# Revit family: ASH_Contour21_S6360_BIM_GB
name_source: partatom
category: Plumbing Fixtures
revit_build: Autodesk Revit MEP 2012 (Build: 20110309_2315(x64)
units: mm (PartAtom-declared; Revit-internal decimal feet)

## types (5) — shared parameters
AccessibilityPerformance = DDA Compliant
Accessories = www.idealspec.co.uk
Assembly Code = C1030200
AssetType = Fixed
BIMObjectName = GRABRAIL_ArmitageShanks_Contour21-Hinged80cm_S6360
Brand = Armitage Shanks
Category = Furntiure_GRABRAIL_UK
ConnectionType = Mechanical
CurrentRevision = 1
Default Elevation = 1219 mm
Description = Contour 21 hinged support rail 80 x 35mm diameter, Doc M Compliant
DurationUnit = Years
ElementType = GRAB RAIL: Safety device to aid maintaining balance, lessen fatigue and assist in supporting weight whilst maneuvering the body
ExpectedLife = 30
Help = http://www.idealspec.co.uk
InstallationInstructions = http://www.idealspec.co.uk
Manufacturer = Ideal Standard International Ltd
ManufacturerURL = www.idealspec.co.uk
Name = GRABRAIL_ArmitageShanks_Contour21-Hinged80cm_S6360
NettWeight = 3.15Kg
NominalHeight = 201 mm
NominalLength = 800 mm  [stored 2.62467 ft]
NominalWidth = 107 mm  [stored 0.35105 ft]
PredefinedType = grabrail
ProductDataSheet = http://www.idealspec.co.uk
ProductInformation = http://www.idealspec.co.uk
S6363AC Required = Yes
SalesInformation = http://www.idealspec.co.uk
SendEnquiry = http://www.idealspec.co.uk
Shape = Tubular
Size = 800mm x 100mm x 200mm
Space = Internal
SpareParts = www.fastpart-spares.co.uk
StandardsConformance = DDA, Doc-M
URL = www.idealspec.co.uk
Version = 2
VolumeUnits = Litres
WarrantyDescription = Manufacturers Warranty
WarrantyDurationParts = 5
WarrantyDurationUnit = Years
WarrantyGuarantorParts = Ideal Standard International Ltd

## per-type parameters (varying)
| type | BREEAM Approved | BarCode | Colour | ECA | Features | Finish | Grade | LRVValue | Material | Model | ModelNumber | ModelReference | RAL | TRHColour | WRAS | WaterEfficientProduct |
| S6360LI | No | 5017830444893 | Powder Coated Aluminium Blue LI | No | hinged support rail 80 x 35mm diameter, Doc M Compliant Blue | Powder Coated Aluminium Blue LI | T6 | 27 | Aluminium | S636036 | S636036 | S636036 | 5011 | GRABRAIL_ArmitageShanks_Contour21-TRHolder-S6363AC : S636336 | No | No |
| S636001 | No | 5017830444909 | Powder Coated Aluminium White 01 | No | hinged support rail 80 x 35mm diameter, Doc M Compliant, white | Powder Coated Aluminium White 01 | T6 | 94 | Alumnium | S6360AC | S6360AC | S6360AC | 9016 | GRABRAIL_ArmitageShanks_Contour21-TRHolder-S6363AC : S6363AC | No | No |
| S6360LJ | No | 5017830444916 | Powder Coated Aluminium Grey LJ | No | hinged support rail 80 x 35mm diameter, Doc M Compliant Light Grey | Powder Coated Aluminium Grey LJ | T6 | 20 | Aluminium | S6360LJ | S6360LJ | S6360LJ | 7005 | GRABRAIL_ArmitageShanks_Contour21-TRHolder-S6363AC : S6363LJ | No | No |
| S6360RN | Yes | 5017830444930 | Powder Coated Aluminium Charcoal RN | Yes | hinged support rail 80 x 35mm diameter, Doc M Compliant Charcoal | Powder Coated Aluminium Charcoal RN | T6 | 9 | Aluminium | S6360RN | S6360RN | S6360RN | 7016 | GRABRAIL_ArmitageShanks_Contour21-TRHolder-S6363AC : S6363RN | Yes | Yes |
| S6360MY | No | 5017830444923 | Stainless Steel MY | No | hinged support rail 80 x 35mm diameter, Doc M Compliant Stainless Steel | Polished | 304 |  | Stainless Steel | S6360MY | S6360MY | S6360MY |  | GRABRAIL_ArmitageShanks_Contour21-TRHolder-S6363AC : S6363LJ | No | No |

note: column(s) folded — value = type name in every type: PartNumber

note: [stored X ft] marks values corroborated as IEEE doubles in the binary element streams (Revit-internal decimal feet)

## geometry (parser evidence)
native form markers: Blend x7, Sweep x4
no freeform markers — native parametric forms only
